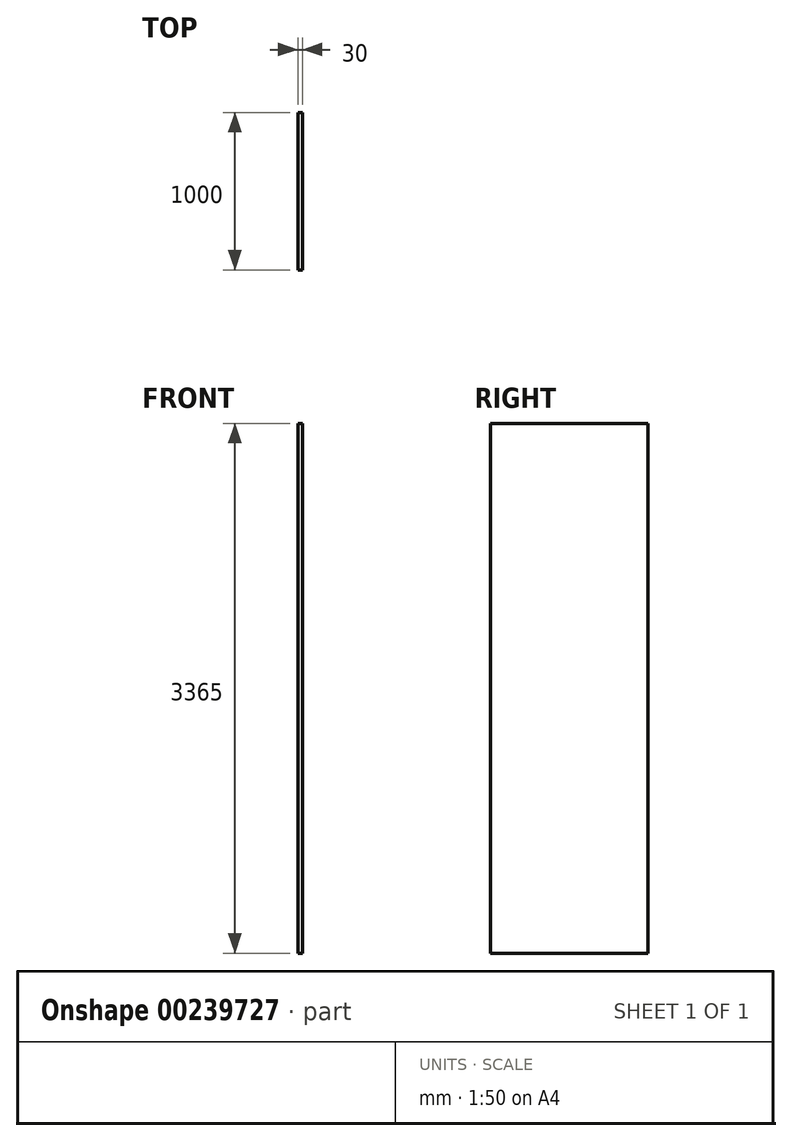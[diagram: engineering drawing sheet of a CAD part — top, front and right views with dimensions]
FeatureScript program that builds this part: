
annotation { "Feature Type Name" : "Feature", "Feature Type Description" : "" }
export const myFeature = defineFeature(function(context is Context, id is Id, definition is map)
    precondition{}
    {
        {
            var Q0;
            Q0=qCreatedBy(makeId("Right.planeOp"),FACE);
            var sketch = newSketch(context, id + "F0", { "sketchPlane" : qUnion([Q0])});
            skLineSegment(sketch, "E0.bottom", {"start": v(0, 0) * mm, "end": v(1000, 0) * mm});
            skLineSegment(sketch, "E0.top", {"start": v(0, 3365) * mm, "end": v(1000, 3365) * mm});
            skLineSegment(sketch, "E0.left", {"start": v(0, 0) * mm, "end": v(0, 3365) * mm});
            skLineSegment(sketch, "E0.right", {"start": v(1000, 0) * mm, "end": v(1000, 3365) * mm});
            skSolve(sketch);
        }
        {
            var Q0;
            Q0=makeQuery(id+"F0.imprint","IMPRINT",FACE,{"disambiguationData":[TD([[makeQuery(id+"F0.imprint","IMPRINT",EDGE,{"derivedFrom":sQuery(id+"F0.wireOp",EDGE,"E0.bottom")}),1.0]])]});
            extrude(context, id + "F1", {"entities" : qUnion([Q0]), "depth" : 30 * mm});
        }
    });
